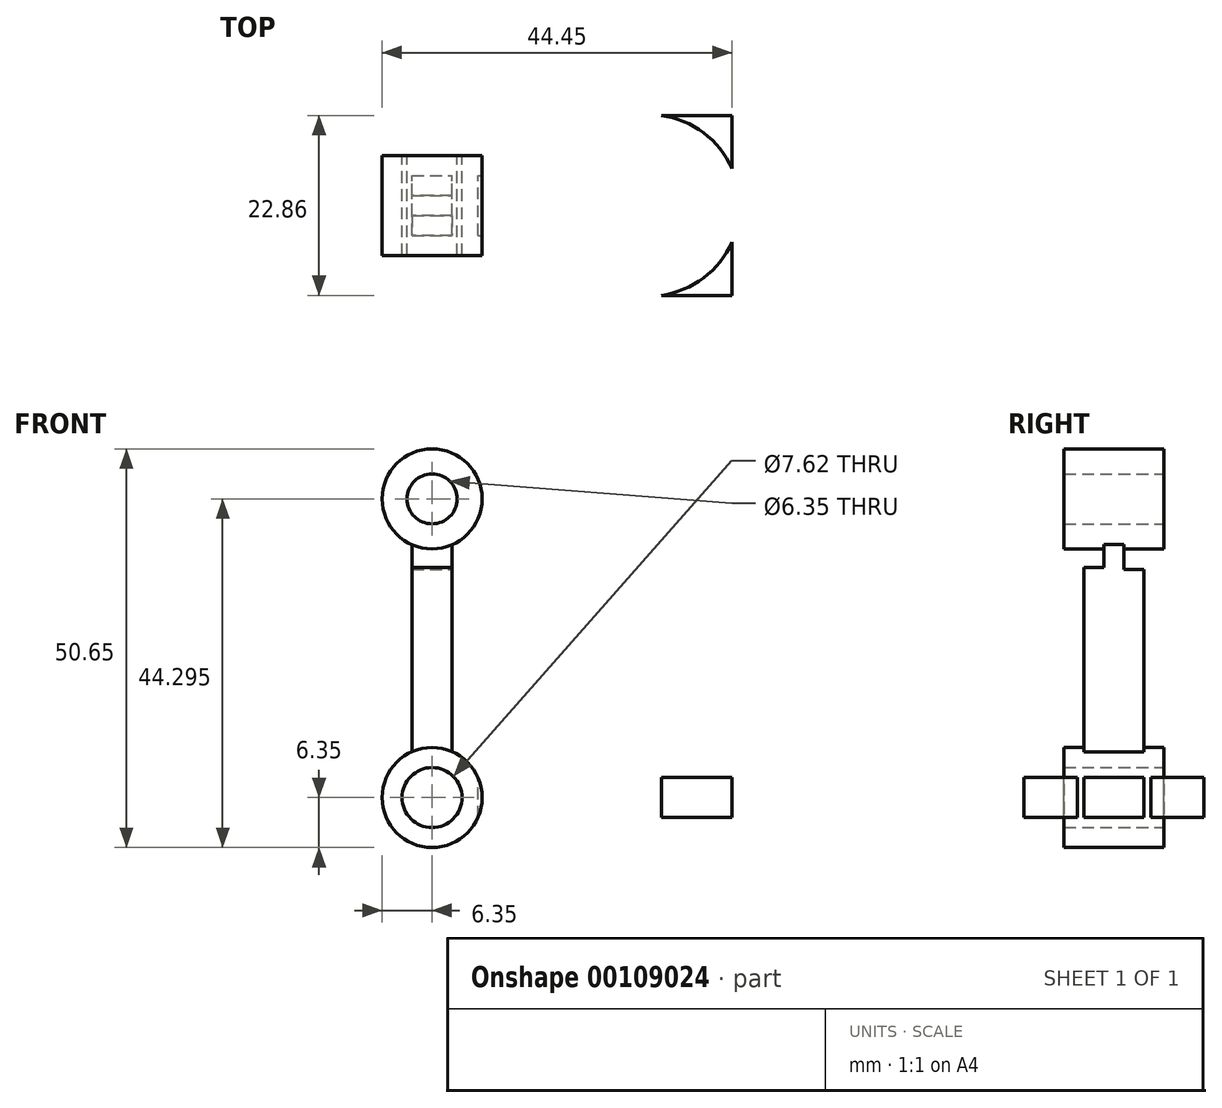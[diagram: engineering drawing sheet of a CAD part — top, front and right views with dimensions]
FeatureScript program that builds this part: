
annotation { "Feature Type Name" : "Feature", "Feature Type Description" : "" }
export const myFeature = defineFeature(function(context is Context, id is Id, definition is map)
    precondition{}
    {
        {
            var Q0;
            Q0=qCreatedBy(makeId("Front.planeOp"),FACE);
            var sketch = newSketch(context, id + "F0", { "sketchPlane" : qUnion([Q0])});
            skCircle(sketch, "E0", {"center": v(0, 0) * mm, "radius": 3.81 * mm});
            skCircle(sketch, "E1", {"center": v(0, 0) * mm, "radius": 6.35 * mm});
            skSolve(sketch);
        }
        {
            var Q0;
            Q0=makeQuery(id+"F0.imprint","IMPRINT",FACE,{"disambiguationData":[TD([[makeQuery(id+"F0.imprint","IMPRINT",EDGE,{"derivedFrom":sQuery(id+"F0.wireOp",EDGE,"E0")}),-1.0]])]});
            extrude(context, id + "F1", {"entities" : qUnion([Q0]), "depth" : 12.7 * mm});
        }
        {
            var Q0;
            Q0=qCreatedBy(makeId("Top.planeOp"),FACE);
            var sketch = newSketch(context, id + "F2", { "sketchPlane" : qUnion([Q0])});
            skLineSegment(sketch, "E2", {"start": v(0, 0) * mm, "end": v(-6.35, 0) * mm});
            skLineSegment(sketch, "E3", {"start": v(-6.35, -6.35) * mm, "end": v(-6.35, -10.16) * mm});
            skLineSegment(sketch, "E4", {"start": v(-6.35, -6.35) * mm, "end": v(-6.35, -2.54) * mm});
            skSolve(sketch);
        }
        {
            var Q0;
            Q0=qCreatedBy(makeId("Right.planeOp"),FACE);
            var sketch = newSketch(context, id + "F3", { "sketchPlane" : qUnion([Q0])});
            skLineSegment(sketch, "E5", {"start": v(-2.54, 0) * mm, "end": v(-2.54, 2.54) * mm});
            skLineSegment(sketch, "E6", {"start": v(-2.54, 0) * mm, "end": v(-2.54, -2.54) * mm});
            skLineSegment(sketch, "E7", {"start": v(-2.54, -2.54) * mm, "end": v(-10.16, -2.54) * mm});
            skLineSegment(sketch, "E8", {"start": v(-10.16, -2.54) * mm, "end": v(-10.16, 0) * mm});
            skLineSegment(sketch, "E9", {"start": v(-10.16, 0) * mm, "end": v(-10.16, 2.54) * mm});
            skLineSegment(sketch, "E10", {"start": v(-10.16, 2.54) * mm, "end": v(-2.54, 2.54) * mm});
            skSolve(sketch);
        }
        {
            var Q0;
            Q0=makeQuery(id+"F3.imprint","IMPRINT",FACE,{"disambiguationData":[TD([[makeQuery(id+"F3.imprint","IMPRINT",EDGE,{"derivedFrom":sQuery(id+"F3.wireOp",EDGE,"E5")}),1.0]])]});
            extrude(context, id + "F4", {"entities" : qUnion([Q0]), "operationType" : NewBodyOperationType.ADD, "depth" : 38.1 * mm});
        }
        {
            var Q0;
            Q0=makeQuery(id+"F0.imprint","IMPRINT",FACE,{"disambiguationData":[TD([[makeQuery(id+"F0.imprint","IMPRINT",EDGE,{"derivedFrom":sQuery(id+"F0.wireOp",EDGE,"E0")}),1.0]])]});
            extrude(context, id + "F5", {"entities" : qUnion([Q0]), "operationType" : NewBodyOperationType.REMOVE, "depth" : 25.4 * mm, "hasSecondDirection" : true, "secondDirectionOppositeDirection" : true, "secondDirectionDepth" : 25.4 * mm});
        }
        {
            var Q0;
            {var subQ1=sQuery(id+"F3.wireOp",EDGE,"E9");var subQ2=sQuery(id+"F3.wireOp",EDGE,"E8");Q0=makeQuery(id+"F4.boolean.opBoolean","SPLIT",FACE,{"disambiguationData":[TD([makeQuery(id+"F1.opExtrude","SWEPT_FACE",FACE,{"disambiguationData":[OSD([sQuery(id+"F0.wireOp",EDGE,"E1")])]})])],"derivedFrom":makeQuery(id+"F4.opExtrude","SWEPT_FACE",FACE,{"disambiguationData":[OSD([subQ2,subQ1])]})});}
            var sketch = newSketch(context, id + "F6", { "sketchPlane" : qUnion([Q0])});
            skLineSegment(sketch, "E11.bottom", {"start": v(24.28, 2.54) * mm, "end": v(38.1, 2.54) * mm});
            skLineSegment(sketch, "E11.top", {"start": v(24.28, -2.54) * mm, "end": v(38.1, -2.54) * mm});
            skLineSegment(sketch, "E11.left", {"start": v(24.28, 2.54) * mm, "end": v(24.28, -2.54) * mm});
            skLineSegment(sketch, "E11.right", {"start": v(38.1, 2.54) * mm, "end": v(38.1, -2.54) * mm});
            skSolve(sketch);
        }
        {
            var Q0;
            Q0=makeQuery(id+"F6.imprint","IMPRINT",FACE,{"disambiguationData":[TD([[makeQuery(id+"F6.imprint","IMPRINT",EDGE,{"derivedFrom":sQuery(id+"F6.wireOp",EDGE,"E11.bottom")}),1.0]])]});
            extrude(context, id + "F7", {"entities" : qUnion([Q0]), "operationType" : NewBodyOperationType.ADD, "depth" : 7.62 * mm, "hasSecondDirection" : true, "secondDirectionOppositeDirection" : true, "secondDirectionDepth" : 15.24 * mm});
        }
        {
            var Q0;
            {var subQ2=sQuery(id+"F6.wireOp",EDGE,"E11.left");Q0=makeQuery(id+"F7.boolean.opBoolean","SPLIT",FACE,{"disambiguationData":[TD([makeQuery(id+"F4.opExtrude","SWEPT_FACE",FACE,{"disambiguationData":[OSD([sQuery(id+"F3.wireOp",EDGE,"E8"),sQuery(id+"F3.wireOp",EDGE,"E9")])]})])],"derivedFrom":makeQuery(id+"F7.opExtrude","SWEPT_FACE",FACE,{"disambiguationData":[OSD([subQ2])]})});}
            extrude(context, id + "F8", {"entities" : qUnion([Q0]), "operationType" : NewBodyOperationType.ADD, "depth" : 7.62 * mm});
        }
        {
            var Q0;
            {var subQ1=sQuery(id+"F6.wireOp",EDGE,"E11.left");Q0=makeQuery(id+"F7.boolean.opBoolean","SPLIT",FACE,{"disambiguationData":[TD([makeQuery(id+"F4.opExtrude","SWEPT_FACE",FACE,{"disambiguationData":[OSD([sQuery(id+"F3.wireOp",EDGE,"E5"),sQuery(id+"F3.wireOp",EDGE,"E6")])]})])],"derivedFrom":makeQuery(id+"F7.opExtrude","SWEPT_FACE",FACE,{"disambiguationData":[OSD([subQ1])]})});}
            extrude(context, id + "F9", {"entities" : qUnion([Q0]), "operationType" : NewBodyOperationType.ADD, "depth" : 7.62 * mm});
        }
        {
            var Q0;
            {var subQ0=sQuery(id+"F6.wireOp",EDGE,"E11.left");var subQ1=sQuery(id+"F6.wireOp",EDGE,"E11.bottom");var subQ2=sQuery(id+"F3.wireOp",EDGE,"E10");var subQ3=sQuery(id+"F3.wireOp",EDGE,"E9");Q0=makeQuery(id+"F9.boolean.opBoolean","MERGE",FACE,{"derivedFrom":[makeQuery(id+"F8.boolean.opBoolean","MERGE",FACE,{"derivedFrom":[makeQuery(id+"F7.boolean.opBoolean","MERGE",FACE,{"derivedFrom":[makeQuery(id+"F4.boolean.opBoolean","SPLIT",FACE,{"disambiguationData":[TD([makeQuery(id+"F1.opExtrude","SWEPT_FACE",FACE,{"disambiguationData":[OSD([sQuery(id+"F0.wireOp",EDGE,"E1")])]})])],"derivedFrom":makeQuery(id+"F4.opExtrude","SWEPT_FACE",FACE,{"disambiguationData":[OSD([subQ2])]})}),makeQuery(id+"F7.opExtrude","SWEPT_FACE",FACE,{"disambiguationData":[OSD([subQ1])]})]}),makeQuery(id+"F8.opExtrude","SWEPT_FACE",FACE,{"disambiguationData":[OSD([subQ3,subQ2,subQ1,subQ0])]})]}),makeQuery(id+"F9.opExtrude","SWEPT_FACE",FACE,{"disambiguationData":[OSD([subQ3,subQ2,subQ1,subQ0])]})]});}
            var sketch = newSketch(context, id + "F10", { "sketchPlane" : qUnion([Q0])});
            skArc(sketch, "E12", {"start": v(16.66, -2.54) * mm, "mid": v(39.08, -6.35) * mm, "end": v(16.66, -10.16) * mm});
            skLineSegment(sketch, "E13", {"start": v(16.66, -2.54) * mm, "end": v(16.66, 5.08) * mm});
            skLineSegment(sketch, "E14", {"start": v(16.66, 5.08) * mm, "end": v(38.1, 5.08) * mm});
            skLineSegment(sketch, "E15", {"start": v(38.1, 5.08) * mm, "end": v(38.1, -17.78) * mm});
            skLineSegment(sketch, "E16", {"start": v(38.1, -17.78) * mm, "end": v(16.66, -17.78) * mm});
            skLineSegment(sketch, "E17", {"start": v(16.66, -17.78) * mm, "end": v(16.66, -10.16) * mm});
            skSolve(sketch);
        }
        {
            var Q0;
            {var subQ0=sQuery(id+"F10.wireOp",EDGE,"E17");Q0=makeQuery(id+"F10.imprint","IMPRINT",FACE,{"disambiguationData":[TD([[makeQuery(id+"F10.imprint","IMPRINT",EDGE,{"derivedFrom":subQ0}),-1.0]])]});}
            var Q1;
            {var subQ0=sQuery(id+"F10.wireOp",EDGE,"E13");Q1=makeQuery(id+"F10.imprint","IMPRINT",FACE,{"disambiguationData":[TD([[makeQuery(id+"F10.imprint","IMPRINT",EDGE,{"derivedFrom":subQ0}),-1.0]])]});}
            var Q2;
            {var subQ0=sQuery(id+"F10.wireOp",EDGE,"E14");var subQ1=sQuery(id+"F10.wireOp",EDGE,"E12");var subQ2=makeQuery(id+"F10.imprint","INTERSECT",VERTEX,{"disambiguationData":[OD(1.0)],"derivedFrom":[subQ1,subQ0]});Q2=makeQuery(id+"F10.imprint","IMPRINT",FACE,{"disambiguationData":[TD([[makeQuery(id+"F10.imprint","IMPRINT",EDGE,{"disambiguationData":[TD([[subQ2,-1.0]])],"derivedFrom":subQ1}),1.0]])]});}
            var Q3;
            {var subQ0=sQuery(id+"F10.wireOp",EDGE,"E15");var subQ1=sQuery(id+"F10.wireOp",EDGE,"E12");var subQ2=makeQuery(id+"F10.imprint","INTERSECT",VERTEX,{"disambiguationData":[OD(1.0)],"derivedFrom":[subQ1,subQ0]});Q3=makeQuery(id+"F10.imprint","IMPRINT",FACE,{"disambiguationData":[TD([[makeQuery(id+"F10.imprint","IMPRINT",EDGE,{"disambiguationData":[TD([[subQ2,-1.0]])],"derivedFrom":subQ1}),1.0]])]});}
            extrude(context, id + "F11", {"entities" : qUnion([Q0, Q1, Q2, Q3]), "operationType" : NewBodyOperationType.REMOVE, "oppositeDirection" : true, "depth" : 25.4 * mm});
        }
        {
            var Q0;
            {var subQ0=sQuery(id+"F10.wireOp",EDGE,"E15");var subQ1=sQuery(id+"F10.wireOp",EDGE,"E12");var subQ2=makeQuery(id+"F10.imprint","INTERSECT",VERTEX,{"disambiguationData":[OD(0.0)],"derivedFrom":[subQ1,subQ0]});Q0=makeQuery(id+"F10.imprint","IMPRINT",FACE,{"disambiguationData":[TD([[makeQuery(id+"F10.imprint","IMPRINT",EDGE,{"disambiguationData":[TD([[subQ2,-1.0]])],"derivedFrom":subQ1}),-1.0]])]});}
            extrude(context, id + "F12", {"entities" : qUnion([Q0]), "operationType" : NewBodyOperationType.ADD, "oppositeDirection" : true, "depth" : 5.08 * mm});
        }
        {
            var Q0;
            Q0=qCreatedBy(makeId("Top.planeOp"),FACE);
            var sketch = newSketch(context, id + "F13", { "sketchPlane" : qUnion([Q0])});
            skLineSegment(sketch, "E18", {"start": v(0, -2.54) * mm, "end": v(-2.54, -2.54) * mm});
            skLineSegment(sketch, "E19", {"start": v(0, -2.54) * mm, "end": v(2.54, -2.54) * mm});
            skLineSegment(sketch, "E20", {"start": v(2.54, -2.54) * mm, "end": v(2.54, -10.16) * mm});
            skLineSegment(sketch, "E21", {"start": v(-2.54, -2.54) * mm, "end": v(-2.54, -10.16) * mm});
            skLineSegment(sketch, "E22", {"start": v(-2.54, -10.16) * mm, "end": v(0, -10.16) * mm});
            skLineSegment(sketch, "E23", {"start": v(0, -10.16) * mm, "end": v(2.54, -10.16) * mm});
            skSolve(sketch);
        }
        {
            var Q0;
            Q0=makeQuery(id+"F13.imprint","IMPRINT",FACE,{"disambiguationData":[TD([[makeQuery(id+"F13.imprint","IMPRINT",EDGE,{"derivedFrom":sQuery(id+"F13.wireOp",EDGE,"E18")}),1.0]])]});
            extrude(context, id + "F14", {"entities" : qUnion([Q0]), "operationType" : NewBodyOperationType.ADD, "depth" : 38.1 * mm});
        }
        {
            var Q0;
            Q0=makeQuery(id+"F0.imprint","IMPRINT",FACE,{"disambiguationData":[TD([[makeQuery(id+"F0.imprint","IMPRINT",EDGE,{"derivedFrom":sQuery(id+"F0.wireOp",EDGE,"E0")}),1.0]])]});
            extrude(context, id + "F15", {"entities" : qUnion([Q0]), "operationType" : NewBodyOperationType.REMOVE, "depth" : 25.4 * mm});
        }
        {
            var Q0;
            {var subQ2=sQuery(id+"F13.wireOp",EDGE,"E19");var subQ3=sQuery(id+"F13.wireOp",EDGE,"E18");Q0=makeQuery(id+"F14.boolean.opBoolean","SPLIT",FACE,{"disambiguationData":[TD([makeQuery(id+"F1.opExtrude","SWEPT_FACE",FACE,{"disambiguationData":[OSD([sQuery(id+"F0.wireOp",EDGE,"E1")])]})])],"derivedFrom":makeQuery(id+"F14.opExtrude","SWEPT_FACE",FACE,{"disambiguationData":[OSD([subQ3,subQ2])]})});}
            var sketch = newSketch(context, id + "F16", { "sketchPlane" : qUnion([Q0])});
            skLineSegment(sketch, "E24", {"start": v(0, 38.1) * mm, "end": v(0, 28.96) * mm});
            skPoint(sketch, "E24.endSnap0", {"position": v(0, 38.1) * mm});
            skLineSegment(sketch, "E25", {"start": v(0, 28.96) * mm, "end": v(-2.54, 28.96) * mm});
            skLineSegment(sketch, "E26", {"start": v(-2.54, 28.96) * mm, "end": v(-2.54, 38.1) * mm});
            skLineSegment(sketch, "E27", {"start": v(-2.54, 38.1) * mm, "end": v(0, 38.1) * mm});
            skLineSegment(sketch, "E28", {"start": v(0, 38.1) * mm, "end": v(2.54, 38.1) * mm});
            skLineSegment(sketch, "E29", {"start": v(2.54, 38.1) * mm, "end": v(2.54, 28.96) * mm});
            skLineSegment(sketch, "E30", {"start": v(0, 28.96) * mm, "end": v(2.54, 28.96) * mm});
            skSolve(sketch);
        }
        {
            var Q0;
            Q0=makeQuery(id+"F16.imprint","IMPRINT",FACE,{"disambiguationData":[TD([[makeQuery(id+"F16.imprint","IMPRINT",EDGE,{"derivedFrom":sQuery(id+"F16.wireOp",EDGE,"E24")}),-1.0]])]});
            var Q1;
            Q1=makeQuery(id+"F16.imprint","IMPRINT",FACE,{"disambiguationData":[TD([[makeQuery(id+"F16.imprint","IMPRINT",EDGE,{"derivedFrom":sQuery(id+"F16.wireOp",EDGE,"E24")}),1.0]])]});
            extrude(context, id + "F17", {"entities" : qUnion([Q0, Q1]), "operationType" : NewBodyOperationType.REMOVE, "oppositeDirection" : true, "depth" : 2.54 * mm});
        }
        {
            var Q0;
            {var subQ0=sQuery(id+"F13.wireOp",EDGE,"E23");var subQ1=sQuery(id+"F13.wireOp",EDGE,"E22");Q0=makeQuery(id+"F14.boolean.opBoolean","SPLIT",FACE,{"disambiguationData":[TD([makeQuery(id+"F1.opExtrude","SWEPT_FACE",FACE,{"disambiguationData":[OSD([sQuery(id+"F0.wireOp",EDGE,"E1")])]})])],"derivedFrom":makeQuery(id+"F14.opExtrude","SWEPT_FACE",FACE,{"disambiguationData":[OSD([subQ1,subQ0])]})});}
            var sketch = newSketch(context, id + "F18", { "sketchPlane" : qUnion([Q0])});
            skLineSegment(sketch, "E31", {"start": v(0, 38.1) * mm, "end": v(0, 29.21) * mm});
            skPoint(sketch, "E31.endSnap0", {"position": v(0, 38.1) * mm});
            skLineSegment(sketch, "E32", {"start": v(0, 29.21) * mm, "end": v(2.54, 29.21) * mm});
            skLineSegment(sketch, "E33", {"start": v(0, 29.21) * mm, "end": v(-2.54, 29.21) * mm});
            skSolve(sketch);
        }
        {
            var Q0;
            {var subQ0=sQuery(id+"F18.wireOp",EDGE,"E31");Q0=makeQuery(id+"F18.imprint","IMPRINT",FACE,{"disambiguationData":[TD([[makeQuery(id+"F18.imprint","IMPRINT",EDGE,{"derivedFrom":subQ0}),-1.0]])]});}
            var Q1;
            {var subQ0=sQuery(id+"F18.wireOp",EDGE,"E31");Q1=makeQuery(id+"F18.imprint","IMPRINT",FACE,{"disambiguationData":[TD([[makeQuery(id+"F18.imprint","IMPRINT",EDGE,{"derivedFrom":subQ0}),1.0]])]});}
            extrude(context, id + "F19", {"entities" : qUnion([Q0, Q1]), "operationType" : NewBodyOperationType.REMOVE, "oppositeDirection" : true, "depth" : 2.54 * mm});
        }
        {
            var Q0;
            Q0=qCreatedBy(makeId("Front.planeOp"),FACE);
            var sketch = newSketch(context, id + "F20", { "sketchPlane" : qUnion([Q0])});
            skCircle(sketch, "E34", {"center": v(0, 37.95) * mm, "radius": 3.18 * mm});
            skLineSegment(sketch, "E35", {"start": v(0, 37.95) * mm, "end": v(0, 0) * mm});
            skCircle(sketch, "E36", {"center": v(0, 37.95) * mm, "radius": 6.35 * mm});
            skSolve(sketch);
        }
        {
            var Q0;
            Q0=makeQuery(id+"F20.imprint","IMPRINT",FACE,{"disambiguationData":[TD([[makeQuery(id+"F20.imprint","IMPRINT",EDGE,{"derivedFrom":sQuery(id+"F20.wireOp",EDGE,"E34")}),1.0]])]});
            extrude(context, id + "F21", {"entities" : qUnion([Q0]), "operationType" : NewBodyOperationType.REMOVE, "depth" : 12.7 * mm});
        }
        {
            var Q0;
            Q0=makeQuery(id+"F20.imprint","IMPRINT",FACE,{"disambiguationData":[TD([[makeQuery(id+"F20.imprint","IMPRINT",EDGE,{"derivedFrom":sQuery(id+"F20.wireOp",EDGE,"E34")}),-1.0]])]});
            extrude(context, id + "F22", {"entities" : qUnion([Q0]), "operationType" : NewBodyOperationType.ADD, "depth" : 12.7 * mm});
        }
    });
